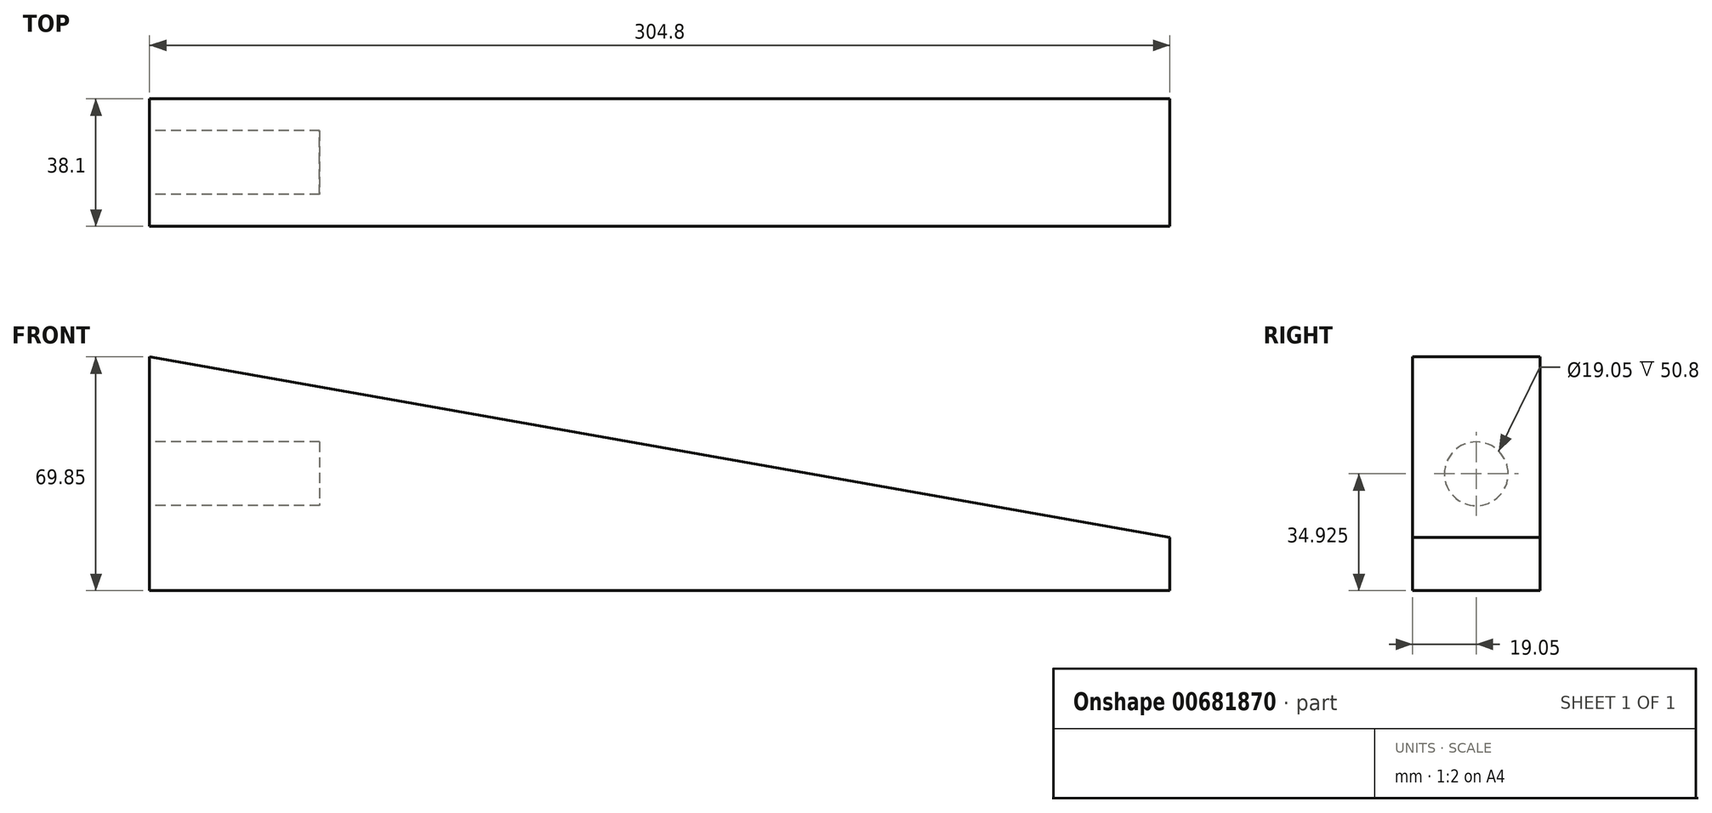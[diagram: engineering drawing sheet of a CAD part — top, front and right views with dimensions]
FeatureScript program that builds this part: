
annotation { "Feature Type Name" : "Feature", "Feature Type Description" : "" }
export const myFeature = defineFeature(function(context is Context, id is Id, definition is map)
    precondition{}
    {
        {
            var Q0;
            Q0=qCreatedBy(makeId("Front.planeOp"),FACE);
            var sketch = newSketch(context, id + "F0", { "sketchPlane" : qUnion([Q0])});
            skLineSegment(sketch, "E0", {"start": v(0, 0) * mm, "end": v(304.8, 0) * mm});
            skLineSegment(sketch, "E1", {"start": v(0, 0) * mm, "end": v(0, 69.85) * mm});
            skLineSegment(sketch, "E2", {"start": v(304.8, 0) * mm, "end": v(304.8, 15.88) * mm});
            skLineSegment(sketch, "E3", {"start": v(0, 69.85) * mm, "end": v(304.8, 15.88) * mm});
            skSolve(sketch);
        }
        {
            var Q0;
            Q0=makeQuery(id+"F0.imprint","IMPRINT",FACE,{"disambiguationData":[TD([[makeQuery(id+"F0.imprint","IMPRINT",EDGE,{"derivedFrom":sQuery(id+"F0.wireOp",EDGE,"E0")}),1.0]])]});
            extrude(context, id + "F1", {"entities" : qUnion([Q0]), "oppositeDirection" : true, "depth" : 38.1 * mm, "offsetDistance" : 25.4 * mm});
        }
        {
            var Q0;
            Q0=makeQuery(id+"F1.opExtrude","SWEPT_FACE",FACE,{"disambiguationData":[OSD([sQuery(id+"F0.wireOp",EDGE,"E1")])]});
            var sketch = newSketch(context, id + "F2", { "sketchPlane" : qUnion([Q0])});
            skPoint(sketch, "E4", {"position": v(-19.05, 34.93) * mm});
            skCircle(sketch, "E5", {"center": v(-19.05, 34.93) * mm, "radius": 9.52 * mm});
            skSolve(sketch);
        }
        {
            var Q0;
            Q0=makeQuery(id+"F2.imprint","IMPRINT",FACE,{"disambiguationData":[TD([[makeQuery(id+"F2.imprint","IMPRINT",EDGE,{"derivedFrom":sQuery(id+"F2.wireOp",EDGE,"E5")}),1.0]])]});
            extrude(context, id + "F3", {"entities" : qUnion([Q0]), "operationType" : NewBodyOperationType.REMOVE, "oppositeDirection" : true, "depth" : 50.8 * mm, "offsetDistance" : 25.4 * mm});
        }
    });
